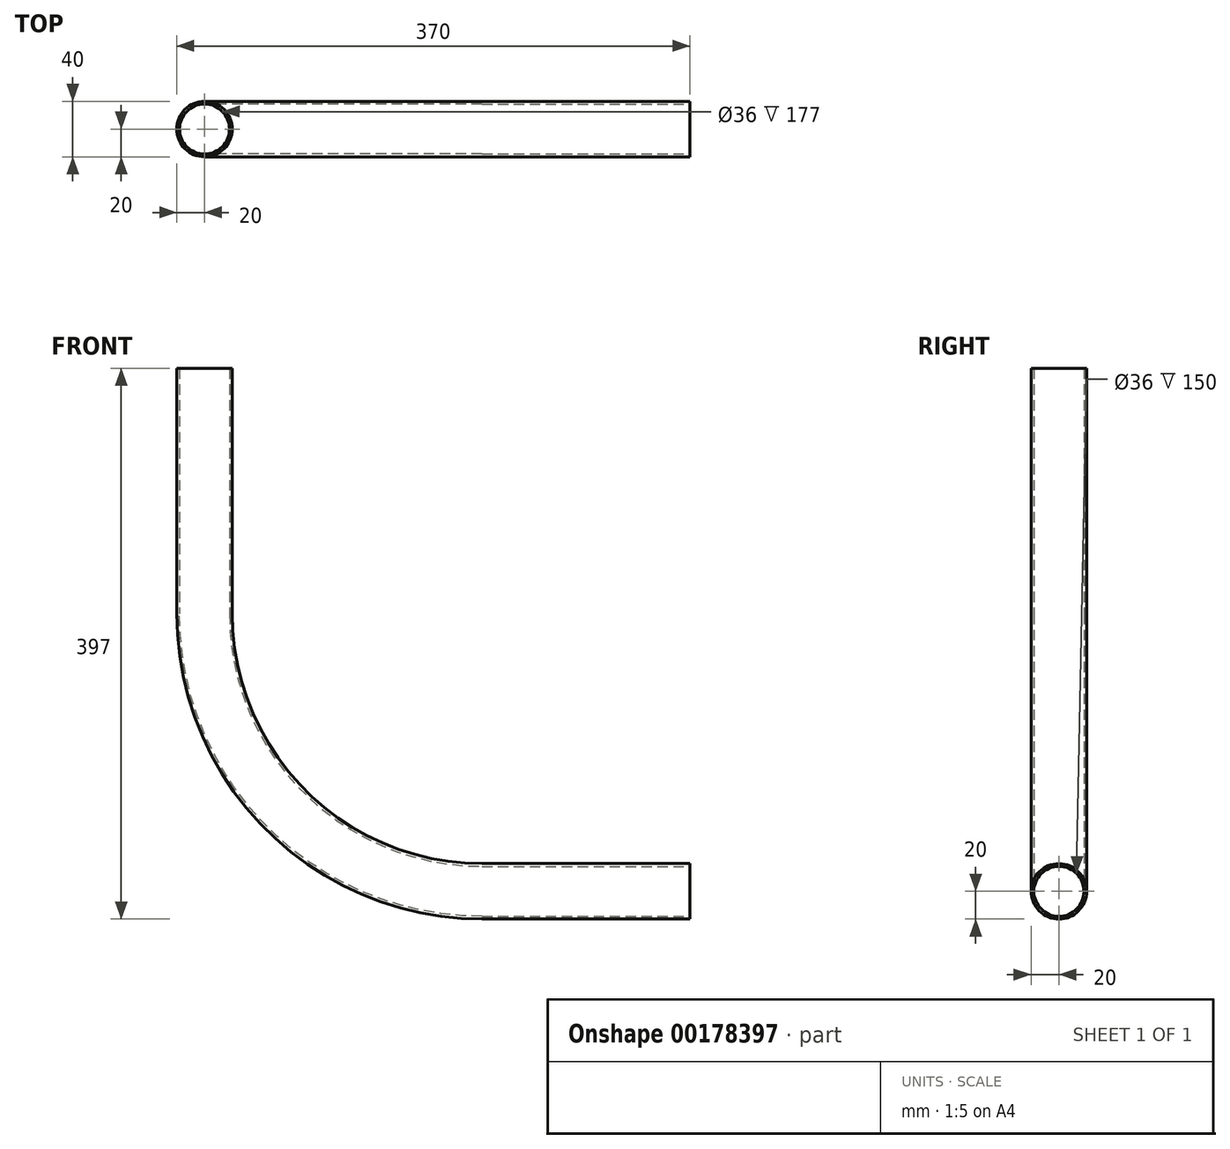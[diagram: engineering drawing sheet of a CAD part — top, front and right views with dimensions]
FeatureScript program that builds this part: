
annotation { "Feature Type Name" : "Feature", "Feature Type Description" : "" }
export const myFeature = defineFeature(function(context is Context, id is Id, definition is map)
    precondition{}
    {
        {
            var Q0;
            Q0=qCreatedBy(makeId("Front.planeOp"),FACE);
            var sketch = newSketch(context, id + "F0", { "sketchPlane" : qUnion([Q0])});
            skLineSegment(sketch, "E0", {"start": v(0, 200) * mm, "end": v(0, 377) * mm});
            skLineSegment(sketch, "E1", {"start": v(200, 0) * mm, "end": v(350, 0) * mm});
            skPoint(sketch, "E2.visualSharp", {"position": v(0, 0) * mm});
            skArc(sketch, "E2.filletArc", {"start": v(0, 200) * mm, "mid": v(58.58, 58.58) * mm, "end": v(200, 0) * mm});
            skSolve(sketch);
        }
        {
            var Q0;
            Q0=sQuery(id+"F0.wireOp",VERTEX,"E0.end");
            var Q1;
            Q1=qCreatedBy(makeId("Top.planeOp"),FACE);
            cPlane(context, id + "F1", {"entities" : qUnion([Q0, Q1]), "cplaneType" : CPlaneType.PLANE_POINT, "offset" : 25 * mm, "width" : 150 * mm, "height" : 150 * mm});
        }
        {
            var Q0;
            Q0=qCreatedBy(id+"F1.planeOp",FACE);
            var sketch = newSketch(context, id + "F2", { "sketchPlane" : qUnion([Q0])});
            skCircle(sketch, "E3", {"center": v(0, 0) * mm, "radius": 20 * mm});
            skCircle(sketch, "E4.0", {"center": v(0, 0) * mm, "radius": 18 * mm});
            skSolve(sketch);
        }
        {
            var Q0;
            Q0=makeQuery(id+"F2.imprint","IMPRINT",FACE,{"disambiguationData":[TD([[makeQuery(id+"F2.imprint","IMPRINT",EDGE,{"derivedFrom":sQuery(id+"F2.wireOp",EDGE,"E3")}),1.0]])]});
            var Q1;
            Q1=sQuery(id+"F0.wireOp",EDGE,"E0");
            var Q2;
            Q2=sQuery(id+"F0.wireOp",EDGE,"E2.filletArc");
            var Q3;
            Q3=sQuery(id+"F0.wireOp",EDGE,"E1");
            sweep(context, id + "F3", {"profiles" : qUnion([Q0]), "path" : qUnion([Q1, Q2, Q3])});
        }
    });
